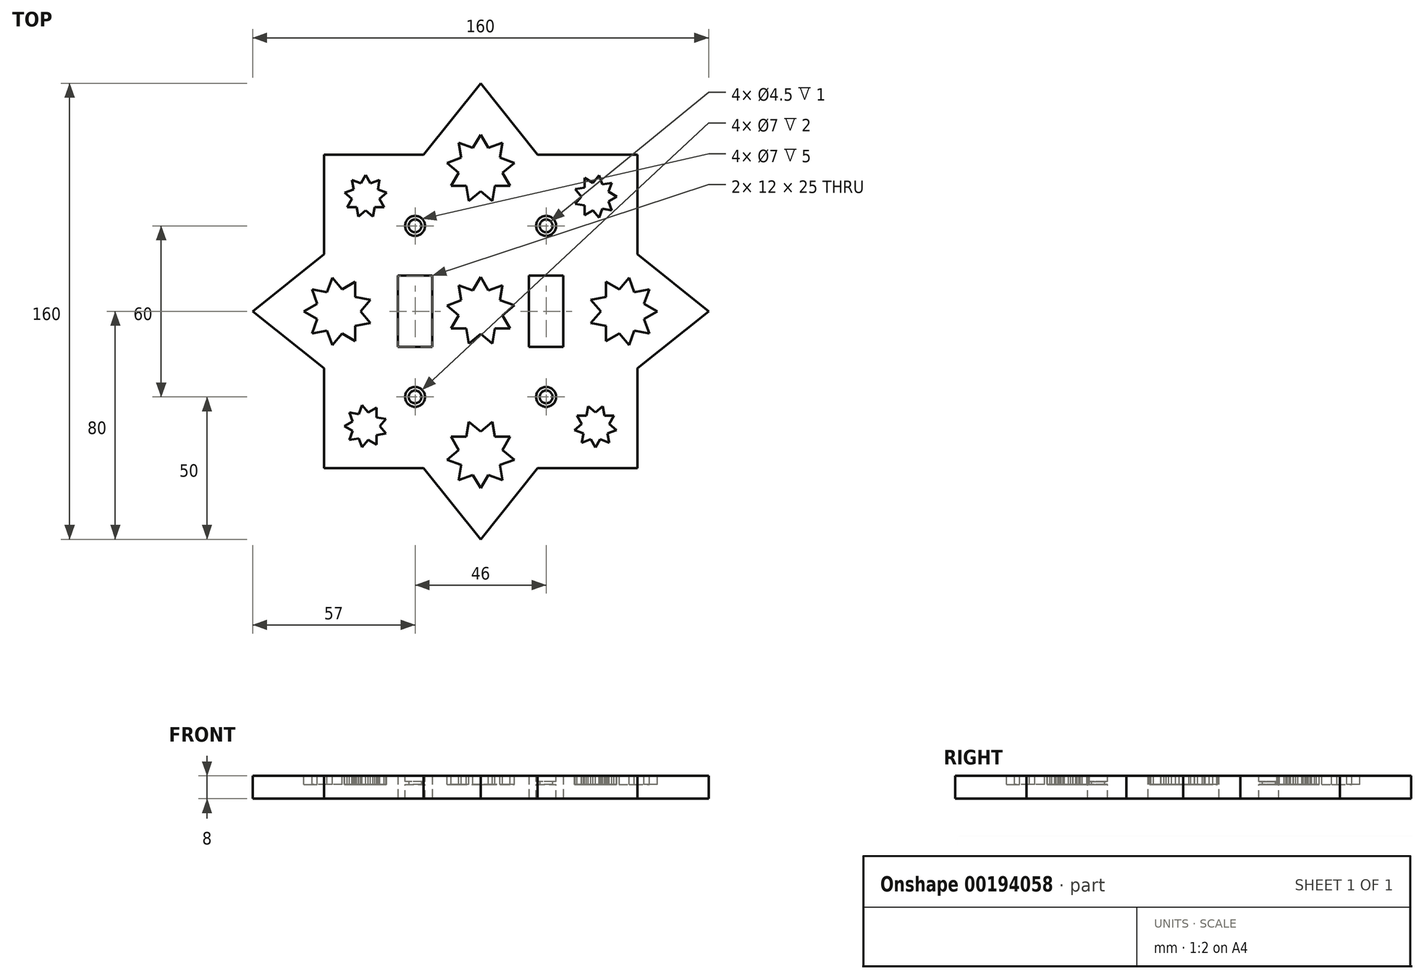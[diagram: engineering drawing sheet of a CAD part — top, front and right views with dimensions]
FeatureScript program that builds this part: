
annotation { "Feature Type Name" : "Feature", "Feature Type Description" : "" }
export const myFeature = defineFeature(function(context is Context, id is Id, definition is map)
    precondition{}
    {
        {
            var Q0;
            Q0=qCreatedBy(makeId("Top.planeOp"),FACE);
            var sketch = newSketch(context, id + "F0", { "sketchPlane" : qUnion([Q0])});
            skLineSegment(sketch, "E0.bottom", {"start": v(55, 55) * mm, "end": v(20, 55) * mm});
            skLineSegment(sketch, "E0.top", {"start": v(55, -55) * mm, "end": v(20, -55) * mm});
            skLineSegment(sketch, "E0.left", {"start": v(55, 55) * mm, "end": v(55, 20) * mm});
            skLineSegment(sketch, "E0.right", {"start": v(-55, 55) * mm, "end": v(-55, 20) * mm});
            skPoint(sketch, "E0.middle", {"position": v(0, 0) * mm});
            skCircle(sketch, "E1", {"center": v(-23, -30) * mm, "radius": 2.25 * mm});
            skCircle(sketch, "E2", {"center": v(-23, 30) * mm, "radius": 2.25 * mm});
            skLineSegment(sketch, "E3.bottom", {"start": v(-29, 12.5) * mm, "end": v(-17, 12.5) * mm});
            skLineSegment(sketch, "E3.top", {"start": v(-29, -12.5) * mm, "end": v(-17, -12.5) * mm});
            skLineSegment(sketch, "E3.left", {"start": v(-29, 12.5) * mm, "end": v(-29, -12.5) * mm});
            skLineSegment(sketch, "E3.right", {"start": v(-17, 12.5) * mm, "end": v(-17, -12.5) * mm});
            skLineSegment(sketch, "E4", {"start": v(-23, 30) * mm, "end": v(-23, -30) * mm, "construction": true});
            skLineSegment(sketch, "E5.MirrorCS", {"start": v(-17, -12.5) * mm, "end": v(-29, -12.5) * mm});
            skLineSegment(sketch, "E6.MirrorCS", {"start": v(-17, 12.5) * mm, "end": v(-29, 12.5) * mm});
            skCircle(sketch, "E7.MirrorC", {"center": v(23, 30) * mm, "radius": 2.25 * mm});
            skLineSegment(sketch, "E8.MirrorCS", {"start": v(29, 12.5) * mm, "end": v(29, -12.5) * mm});
            skLineSegment(sketch, "E9.MirrorCS", {"start": v(17, -12.5) * mm, "end": v(29, -12.5) * mm});
            skCircle(sketch, "E10.MirrorC", {"center": v(23, -30) * mm, "radius": 2.25 * mm});
            skLineSegment(sketch, "E11.MirrorCS", {"start": v(17, 12.5) * mm, "end": v(29, 12.5) * mm});
            skLineSegment(sketch, "E12.MirrorCS", {"start": v(17, 12.5) * mm, "end": v(17, -12.5) * mm});
            skLineSegment(sketch, "E13.MirrorCS", {"start": v(29, -12.5) * mm, "end": v(17, -12.5) * mm});
            skLineSegment(sketch, "E14.MirrorCS", {"start": v(29, 12.5) * mm, "end": v(17, 12.5) * mm});
            skLineSegment(sketch, "E15.MirrorCS", {"start": v(23, 30) * mm, "end": v(23, -30) * mm, "construction": true});
            skLineSegment(sketch, "E16", {"start": v(55, 20) * mm, "end": v(80, 0) * mm});
            skLineSegment(sketch, "E17", {"start": v(-20, 55) * mm, "end": v(0, 80) * mm});
            skLineSegment(sketch, "E18", {"start": v(0, 80) * mm, "end": v(20, 55) * mm});
            skLineSegment(sketch, "E19.MirrorCS", {"start": v(-20, -55) * mm, "end": v(0, -80) * mm});
            skLineSegment(sketch, "E20.MirrorCS", {"start": v(0, -80) * mm, "end": v(20, -55) * mm});
            skLineSegment(sketch, "E21.MirrorCS", {"start": v(55, -20) * mm, "end": v(80, 0) * mm});
            skLineSegment(sketch, "E22.MirrorCS", {"start": v(-55, 20) * mm, "end": v(-80, 0) * mm});
            skLineSegment(sketch, "E23.MirrorCS", {"start": v(-55, -20) * mm, "end": v(-80, 0) * mm});
            skLineSegment(sketch, "E24.trimOffspring", {"start": v(-55, -20) * mm, "end": v(-55, -55) * mm});
            skLineSegment(sketch, "E25.trimOffspring", {"start": v(55, -20) * mm, "end": v(55, -55) * mm});
            skLineSegment(sketch, "E26.trimOffspring", {"start": v(-20, -55) * mm, "end": v(-55, -55) * mm});
            skLineSegment(sketch, "E27.trimOffspring", {"start": v(-20, 55) * mm, "end": v(-55, 55) * mm});
            skPoint(sketch, "E28.MirrorCS.end.orphan", {"position": v(55, 34.57) * mm});
            skPoint(sketch, "E28.MirrorCS.start.orphan", {"position": v(80, 0) * mm});
            skPoint(sketch, "E29.orphan", {"position": v(55, -34.57) * mm});
            skSolve(sketch);
        }
        {
            var Q0;
            Q0 = qSketchRegion(id + "F0", true);
            extrude(context, id + "F1", {"entities" : qUnion([Q0]), "depth" : 3 * mm});
        }
        {
            var Q0;
            Q0=makeQuery(id+"F1.opExtrude","CAP_FACE",FACE,{"disambiguationData":[OSD([sQuery(id+"F0.wireOp",EDGE,"E0.bottom"),sQuery(id+"F0.wireOp",EDGE,"E0.top"),sQuery(id+"F0.wireOp",EDGE,"E0.left"),sQuery(id+"F0.wireOp",EDGE,"E0.right"),sQuery(id+"F0.wireOp",EDGE,"E1"),sQuery(id+"F0.wireOp",EDGE,"E2"),sQuery(id+"F0.wireOp",EDGE,"E3.right"),sQuery(id+"F0.wireOp",EDGE,"E5.MirrorCS"),sQuery(id+"F0.wireOp",EDGE,"E3.left"),sQuery(id+"F0.wireOp",EDGE,"E6.MirrorCS"),sQuery(id+"F0.wireOp",EDGE,"E10.MirrorC"),sQuery(id+"F0.wireOp",EDGE,"E14.MirrorCS"),sQuery(id+"F0.wireOp",EDGE,"E7.MirrorC"),sQuery(id+"F0.wireOp",EDGE,"E8.MirrorCS"),sQuery(id+"F0.wireOp",EDGE,"E9.MirrorCS"),sQuery(id+"F0.wireOp",EDGE,"E12.MirrorCS"),sQuery(id+"F0.wireOp",EDGE,"E16"),sQuery(id+"F0.wireOp",EDGE,"E17"),sQuery(id+"F0.wireOp",EDGE,"E18"),sQuery(id+"F0.wireOp",EDGE,"E19.MirrorCS"),sQuery(id+"F0.wireOp",EDGE,"E20.MirrorCS"),sQuery(id+"F0.wireOp",EDGE,"E21.MirrorCS"),sQuery(id+"F0.wireOp",EDGE,"E22.MirrorCS"),sQuery(id+"F0.wireOp",EDGE,"E23.MirrorCS"),sQuery(id+"F0.wireOp",EDGE,"E24.trimOffspring"),sQuery(id+"F0.wireOp",EDGE,"E25.trimOffspring"),sQuery(id+"F0.wireOp",EDGE,"E26.trimOffspring"),sQuery(id+"F0.wireOp",EDGE,"E27.trimOffspring")])],"isStart":false});
            var sketch = newSketch(context, id + "F2", { "sketchPlane" : qUnion([Q0])});
            skCircle(sketch, "E30.cCircle", {"center": v(0, 50) * mm, "radius": 6 * mm, "construction": true});
            skLineSegment(sketch, "E30.0", {"start": v(-10.4, 44) * mm, "end": v(-7.71, 48.64) * mm});
            skLineSegment(sketch, "E30.1", {"start": v(0, 62) * mm, "end": v(2.68, 57.36) * mm});
            skLineSegment(sketch, "E30.2", {"start": v(10.4, 44) * mm, "end": v(5.03, 44) * mm});
            skPoint(sketch, "E30.0.midPoint", {"position": v(-5.2, 53) * mm});
            skArc(sketch, "E31.cCircle", {"start": v(5.9, 48.96) * mm, "mid": v(-3.86, 54.6) * mm, "end": v(0, 44) * mm, "construction": true});
            skLineSegment(sketch, "E31.0", {"start": v(-11.82, 52.08) * mm, "end": v(-6.78, 53.92) * mm});
            skLineSegment(sketch, "E31.1", {"start": v(7.71, 59.2) * mm, "end": v(6.78, 53.92) * mm});
            skLineSegment(sketch, "E31.2", {"start": v(4.1, 38.72) * mm, "end": v(0, 42.17) * mm});
            skPoint(sketch, "E31.0.midPoint", {"position": v(-2.05, 55.64) * mm});
            skArc(sketch, "E32.cCircle", {"start": v(2.05, 55.64) * mm, "mid": v(0, 56) * mm, "end": v(-2.05, 55.64) * mm, "construction": true});
            skLineSegment(sketch, "E32.0", {"start": v(-7.71, 59.2) * mm, "end": v(-2.68, 57.36) * mm});
            skLineSegment(sketch, "E32.1", {"start": v(11.82, 52.08) * mm, "end": v(7.71, 48.64) * mm});
            skLineSegment(sketch, "E32.2", {"start": v(-4.1, 38.72) * mm, "end": v(-5.03, 44) * mm});
            skPoint(sketch, "E32.0.midPoint", {"position": v(2.05, 55.64) * mm});
            skLineSegment(sketch, "E33", {"start": v(0, 50) * mm, "end": v(0, 121.63) * mm, "construction": true});
            skLineSegment(sketch, "E34.trimOffspring", {"start": v(7.71, 48.64) * mm, "end": v(10.4, 44) * mm});
            skLineSegment(sketch, "E35.trimOffspring", {"start": v(6.78, 53.92) * mm, "end": v(11.82, 52.08) * mm});
            skLineSegment(sketch, "E36.trimOffspring", {"start": v(2.68, 57.36) * mm, "end": v(7.71, 59.2) * mm});
            skLineSegment(sketch, "E37.trimOffspring", {"start": v(-2.68, 57.36) * mm, "end": v(0, 62) * mm});
            skArc(sketch, "E38.trimOffspring", {"start": v(-5.2, 53) * mm, "mid": v(0, 44) * mm, "end": v(5.2, 53) * mm, "construction": true});
            skLineSegment(sketch, "E39.trimOffspring", {"start": v(-6.78, 53.92) * mm, "end": v(-7.71, 59.2) * mm});
            skLineSegment(sketch, "E40.trimOffspring", {"start": v(-7.71, 48.64) * mm, "end": v(-11.82, 52.08) * mm});
            skLineSegment(sketch, "E41.trimOffspring", {"start": v(-5.03, 44) * mm, "end": v(-10.4, 44) * mm});
            skLineSegment(sketch, "E42.trimOffspring", {"start": v(0, 42.17) * mm, "end": v(-4.1, 38.72) * mm});
            skLineSegment(sketch, "E43.trimOffspring", {"start": v(5.03, 44) * mm, "end": v(4.1, 38.72) * mm});
            skLineSegment(sketch, "E44.1.0", {"start": v(-59.2, -7.71) * mm, "end": v(-57.36, -2.68) * mm});
            skLineSegment(sketch, "E44.1.1", {"start": v(-59.2, 7.71) * mm, "end": v(-53.92, 6.78) * mm});
            skLineSegment(sketch, "E44.1.2", {"start": v(-48.64, 7.71) * mm, "end": v(-44, 10.4) * mm});
            skPoint(sketch, "E44.1.3", {"position": v(-55.64, -2.05) * mm});
            skLineSegment(sketch, "E44.1.4", {"start": v(-52.08, -11.82) * mm, "end": v(-53.92, -6.78) * mm});
            skLineSegment(sketch, "E44.1.5", {"start": v(-44, -5.03) * mm, "end": v(-44, -10.4) * mm});
            skArc(sketch, "E44.1.6", {"start": v(-48.96, 5.9) * mm, "mid": v(-54.6, -3.86) * mm, "end": v(-44, 0) * mm, "construction": true});
            skLineSegment(sketch, "E44.1.7", {"start": v(-53.92, 6.78) * mm, "end": v(-52.08, 11.82) * mm});
            skPoint(sketch, "E44.1.8", {"position": v(-53, -5.2) * mm});
            skLineSegment(sketch, "E44.1.9", {"start": v(-44, 10.4) * mm, "end": v(-44, 5.03) * mm});
            skLineSegment(sketch, "E44.1.10", {"start": v(-48.64, -7.71) * mm, "end": v(-52.08, -11.82) * mm});
            skLineSegment(sketch, "E44.1.11", {"start": v(-44, -10.4) * mm, "end": v(-48.64, -7.71) * mm});
            skCircle(sketch, "E44.1.12", {"center": v(-50, 0) * mm, "radius": 6 * mm, "construction": true});
            skLineSegment(sketch, "E44.1.13", {"start": v(-38.72, -4.1) * mm, "end": v(-44, -5.03) * mm});
            skLineSegment(sketch, "E44.1.14", {"start": v(-44, 5.03) * mm, "end": v(-38.72, 4.1) * mm});
            skLineSegment(sketch, "E44.1.15", {"start": v(-57.36, 2.68) * mm, "end": v(-59.2, 7.71) * mm});
            skLineSegment(sketch, "E44.1.16", {"start": v(-42.17, 0) * mm, "end": v(-38.72, -4.1) * mm});
            skLineSegment(sketch, "E44.1.17", {"start": v(-52.08, 11.82) * mm, "end": v(-48.64, 7.71) * mm});
            skPoint(sketch, "E44.1.18", {"position": v(-55.64, 2.05) * mm});
            skArc(sketch, "E44.1.19", {"start": v(-55.64, 2.05) * mm, "mid": v(-56, 0) * mm, "end": v(-55.64, -2.05) * mm, "construction": true});
            skArc(sketch, "E44.1.20", {"start": v(-53, -5.2) * mm, "mid": v(-44, 0) * mm, "end": v(-53, 5.2) * mm, "construction": true});
            skLineSegment(sketch, "E44.1.21", {"start": v(-62, 0) * mm, "end": v(-57.36, 2.68) * mm});
            skLineSegment(sketch, "E44.1.22", {"start": v(-53.92, -6.78) * mm, "end": v(-59.2, -7.71) * mm});
            skLineSegment(sketch, "E44.1.23", {"start": v(-57.36, -2.68) * mm, "end": v(-62, 0) * mm});
            skLineSegment(sketch, "E44.1.24", {"start": v(-38.72, 4.1) * mm, "end": v(-42.17, 0) * mm});
            skLineSegment(sketch, "E44.2.0", {"start": v(7.71, -59.2) * mm, "end": v(2.68, -57.36) * mm});
            skLineSegment(sketch, "E44.2.1", {"start": v(-7.71, -59.2) * mm, "end": v(-6.78, -53.92) * mm});
            skLineSegment(sketch, "E44.2.2", {"start": v(-7.71, -48.64) * mm, "end": v(-10.4, -44) * mm});
            skPoint(sketch, "E44.2.3", {"position": v(2.05, -55.64) * mm});
            skLineSegment(sketch, "E44.2.4", {"start": v(11.82, -52.08) * mm, "end": v(6.78, -53.92) * mm});
            skLineSegment(sketch, "E44.2.5", {"start": v(5.03, -44) * mm, "end": v(10.4, -44) * mm});
            skArc(sketch, "E44.2.6", {"start": v(-5.9, -48.96) * mm, "mid": v(3.86, -54.6) * mm, "end": v(0, -44) * mm, "construction": true});
            skLineSegment(sketch, "E44.2.7", {"start": v(-6.78, -53.92) * mm, "end": v(-11.82, -52.08) * mm});
            skPoint(sketch, "E44.2.8", {"position": v(5.2, -53) * mm});
            skLineSegment(sketch, "E44.2.9", {"start": v(-10.4, -44) * mm, "end": v(-5.03, -44) * mm});
            skLineSegment(sketch, "E44.2.10", {"start": v(7.71, -48.64) * mm, "end": v(11.82, -52.08) * mm});
            skLineSegment(sketch, "E44.2.11", {"start": v(10.4, -44) * mm, "end": v(7.71, -48.64) * mm});
            skCircle(sketch, "E44.2.12", {"center": v(0, -50) * mm, "radius": 6 * mm, "construction": true});
            skLineSegment(sketch, "E44.2.13", {"start": v(4.1, -38.72) * mm, "end": v(5.03, -44) * mm});
            skLineSegment(sketch, "E44.2.14", {"start": v(-5.03, -44) * mm, "end": v(-4.1, -38.72) * mm});
            skLineSegment(sketch, "E44.2.15", {"start": v(-2.68, -57.36) * mm, "end": v(-7.71, -59.2) * mm});
            skLineSegment(sketch, "E44.2.16", {"start": v(0, -42.17) * mm, "end": v(4.1, -38.72) * mm});
            skLineSegment(sketch, "E44.2.17", {"start": v(-11.82, -52.08) * mm, "end": v(-7.71, -48.64) * mm});
            skPoint(sketch, "E44.2.18", {"position": v(-2.05, -55.64) * mm});
            skArc(sketch, "E44.2.19", {"start": v(-2.05, -55.64) * mm, "mid": v(0, -56) * mm, "end": v(2.05, -55.64) * mm, "construction": true});
            skArc(sketch, "E44.2.20", {"start": v(5.2, -53) * mm, "mid": v(0, -44) * mm, "end": v(-5.2, -53) * mm, "construction": true});
            skLineSegment(sketch, "E44.2.21", {"start": v(0, -62) * mm, "end": v(-2.68, -57.36) * mm});
            skLineSegment(sketch, "E44.2.22", {"start": v(6.78, -53.92) * mm, "end": v(7.71, -59.2) * mm});
            skLineSegment(sketch, "E44.2.23", {"start": v(2.68, -57.36) * mm, "end": v(0, -62) * mm});
            skLineSegment(sketch, "E44.2.24", {"start": v(-4.1, -38.72) * mm, "end": v(0, -42.17) * mm});
            skLineSegment(sketch, "E44.3.0", {"start": v(59.2, 7.71) * mm, "end": v(57.36, 2.68) * mm});
            skLineSegment(sketch, "E44.3.1", {"start": v(59.2, -7.71) * mm, "end": v(53.92, -6.78) * mm});
            skLineSegment(sketch, "E44.3.2", {"start": v(48.64, -7.71) * mm, "end": v(44, -10.4) * mm});
            skPoint(sketch, "E44.3.3", {"position": v(55.64, 2.05) * mm});
            skLineSegment(sketch, "E44.3.4", {"start": v(52.08, 11.82) * mm, "end": v(53.92, 6.78) * mm});
            skLineSegment(sketch, "E44.3.5", {"start": v(44, 5.03) * mm, "end": v(44, 10.4) * mm});
            skArc(sketch, "E44.3.6", {"start": v(48.96, -5.9) * mm, "mid": v(54.6, 3.86) * mm, "end": v(44, 0) * mm, "construction": true});
            skLineSegment(sketch, "E44.3.7", {"start": v(53.92, -6.78) * mm, "end": v(52.08, -11.82) * mm});
            skPoint(sketch, "E44.3.8", {"position": v(53, 5.2) * mm});
            skLineSegment(sketch, "E44.3.9", {"start": v(44, -10.4) * mm, "end": v(44, -5.03) * mm});
            skLineSegment(sketch, "E44.3.10", {"start": v(48.64, 7.71) * mm, "end": v(52.08, 11.82) * mm});
            skLineSegment(sketch, "E44.3.11", {"start": v(44, 10.4) * mm, "end": v(48.64, 7.71) * mm});
            skCircle(sketch, "E44.3.12", {"center": v(50, 0) * mm, "radius": 6 * mm, "construction": true});
            skLineSegment(sketch, "E44.3.13", {"start": v(38.72, 4.1) * mm, "end": v(44, 5.03) * mm});
            skLineSegment(sketch, "E44.3.14", {"start": v(44, -5.03) * mm, "end": v(38.72, -4.1) * mm});
            skLineSegment(sketch, "E44.3.15", {"start": v(57.36, -2.68) * mm, "end": v(59.2, -7.71) * mm});
            skLineSegment(sketch, "E44.3.16", {"start": v(42.17, 0) * mm, "end": v(38.72, 4.1) * mm});
            skLineSegment(sketch, "E44.3.17", {"start": v(52.08, -11.82) * mm, "end": v(48.64, -7.71) * mm});
            skPoint(sketch, "E44.3.18", {"position": v(55.64, -2.05) * mm});
            skArc(sketch, "E44.3.19", {"start": v(55.64, -2.05) * mm, "mid": v(56, 0) * mm, "end": v(55.64, 2.05) * mm, "construction": true});
            skArc(sketch, "E44.3.20", {"start": v(53, 5.2) * mm, "mid": v(44, 0) * mm, "end": v(53, -5.2) * mm, "construction": true});
            skLineSegment(sketch, "E44.3.21", {"start": v(62, 0) * mm, "end": v(57.36, -2.68) * mm});
            skLineSegment(sketch, "E44.3.22", {"start": v(53.92, 6.78) * mm, "end": v(59.2, 7.71) * mm});
            skLineSegment(sketch, "E44.3.23", {"start": v(57.36, 2.68) * mm, "end": v(62, 0) * mm});
            skLineSegment(sketch, "E44.3.24", {"start": v(38.72, -4.1) * mm, "end": v(42.17, 0) * mm});
            skPoint(sketch, "E44.center", {"position": v(0, 0) * mm});
            skCircle(sketch, "E45.cCircle", {"center": v(-40.3, 40.3) * mm, "radius": 3.75 * mm, "construction": true});
            skLineSegment(sketch, "E45.0", {"start": v(-46.8, 36.56) * mm, "end": v(-45.13, 39.46) * mm});
            skLineSegment(sketch, "E45.1", {"start": v(-40.3, 47.8) * mm, "end": v(-38.63, 44.9) * mm});
            skLineSegment(sketch, "E45.2", {"start": v(-33.8, 36.56) * mm, "end": v(-37.16, 36.56) * mm});
            skPoint(sketch, "E45.0.midPoint", {"position": v(-43.55, 42.18) * mm});
            skArc(sketch, "E46.cCircle", {"start": v(-36.61, 39.65) * mm, "mid": v(-43.7, 41.9) * mm, "end": v(-37.43, 37.9) * mm, "construction": true});
            skLineSegment(sketch, "E46.0", {"start": v(-47.7, 41.6) * mm, "end": v(-44.54, 42.75) * mm});
            skLineSegment(sketch, "E46.1", {"start": v(-35.48, 46.05) * mm, "end": v(-36.07, 42.75) * mm});
            skLineSegment(sketch, "E46.2", {"start": v(-37.74, 33.26) * mm, "end": v(-40.3, 35.4) * mm});
            skPoint(sketch, "E46.0.midPoint", {"position": v(-41.59, 43.83) * mm});
            skArc(sketch, "E47.cCircle", {"start": v(-39.02, 43.83) * mm, "mid": v(-40.3, 44.06) * mm, "end": v(-41.59, 43.83) * mm, "construction": true});
            skLineSegment(sketch, "E47.0", {"start": v(-45.13, 46.05) * mm, "end": v(-41.98, 44.9) * mm});
            skLineSegment(sketch, "E47.1", {"start": v(-32.92, 41.6) * mm, "end": v(-35.48, 39.46) * mm});
            skLineSegment(sketch, "E47.2", {"start": v(-42.87, 33.26) * mm, "end": v(-43.45, 36.56) * mm});
            skPoint(sketch, "E47.0.midPoint", {"position": v(-39.02, 43.83) * mm});
            skLineSegment(sketch, "E48", {"start": v(-40.3, 40.3) * mm, "end": v(-40.3, 75.93) * mm, "construction": true});
            skLineSegment(sketch, "E49.trimOffspring", {"start": v(-35.48, 39.46) * mm, "end": v(-33.8, 36.56) * mm});
            skLineSegment(sketch, "E50.trimOffspring", {"start": v(-36.07, 42.75) * mm, "end": v(-32.92, 41.6) * mm});
            skLineSegment(sketch, "E51.trimOffspring", {"start": v(-38.63, 44.9) * mm, "end": v(-35.48, 46.05) * mm});
            skLineSegment(sketch, "E52.trimOffspring", {"start": v(-41.98, 44.9) * mm, "end": v(-40.3, 47.8) * mm});
            skArc(sketch, "E53.trimOffspring", {"start": v(-43.55, 42.18) * mm, "mid": v(-40.3, 36.56) * mm, "end": v(-37.06, 42.18) * mm, "construction": true});
            skLineSegment(sketch, "E54.trimOffspring", {"start": v(-44.54, 42.75) * mm, "end": v(-45.13, 46.05) * mm});
            skLineSegment(sketch, "E55.trimOffspring", {"start": v(-45.13, 39.46) * mm, "end": v(-47.7, 41.6) * mm});
            skLineSegment(sketch, "E56.trimOffspring", {"start": v(-43.45, 36.56) * mm, "end": v(-46.8, 36.56) * mm});
            skLineSegment(sketch, "E57.trimOffspring", {"start": v(-40.3, 35.4) * mm, "end": v(-42.87, 33.26) * mm});
            skLineSegment(sketch, "E58.trimOffspring", {"start": v(-37.16, 36.56) * mm, "end": v(-37.74, 33.26) * mm});
            skLineSegment(sketch, "E59", {"start": v(0, 0) * mm, "end": v(-55, 55) * mm, "construction": true});
            skLineSegment(sketch, "E60.1.0", {"start": v(-39.46, -45.13) * mm, "end": v(-41.6, -47.7) * mm});
            skLineSegment(sketch, "E60.1.1", {"start": v(-44.9, -38.63) * mm, "end": v(-46.05, -35.48) * mm});
            skPoint(sketch, "E60.1.2", {"position": v(-43.83, -39.02) * mm});
            skCircle(sketch, "E60.1.3", {"center": v(-40.3, -40.3) * mm, "radius": 3.75 * mm, "construction": true});
            skLineSegment(sketch, "E60.1.4", {"start": v(-41.6, -32.92) * mm, "end": v(-39.46, -35.48) * mm});
            skLineSegment(sketch, "E60.1.5", {"start": v(-46.05, -45.13) * mm, "end": v(-44.9, -41.98) * mm});
            skLineSegment(sketch, "E60.1.6", {"start": v(-44.9, -41.98) * mm, "end": v(-47.8, -40.3) * mm});
            skLineSegment(sketch, "E60.1.7", {"start": v(-36.56, -46.8) * mm, "end": v(-39.46, -45.13) * mm});
            skLineSegment(sketch, "E60.1.8", {"start": v(0, 0) * mm, "end": v(-55, -55) * mm, "construction": true});
            skLineSegment(sketch, "E60.1.9", {"start": v(-36.56, -33.8) * mm, "end": v(-36.56, -37.16) * mm});
            skLineSegment(sketch, "E60.1.10", {"start": v(-33.26, -37.74) * mm, "end": v(-35.4, -40.3) * mm});
            skLineSegment(sketch, "E60.1.11", {"start": v(-36.56, -37.16) * mm, "end": v(-33.26, -37.74) * mm});
            skLineSegment(sketch, "E60.1.12", {"start": v(-41.6, -47.7) * mm, "end": v(-42.75, -44.54) * mm});
            skLineSegment(sketch, "E60.1.13", {"start": v(-46.05, -35.48) * mm, "end": v(-42.75, -36.07) * mm});
            skLineSegment(sketch, "E60.1.14", {"start": v(-39.46, -35.48) * mm, "end": v(-36.56, -33.8) * mm});
            skLineSegment(sketch, "E60.1.15", {"start": v(-42.75, -36.07) * mm, "end": v(-41.6, -32.92) * mm});
            skPoint(sketch, "E60.1.16", {"position": v(-42.18, -43.55) * mm});
            skLineSegment(sketch, "E60.1.17", {"start": v(-40.3, -40.3) * mm, "end": v(-75.93, -40.3) * mm, "construction": true});
            skPoint(sketch, "E60.1.18", {"position": v(-43.83, -41.59) * mm});
            skLineSegment(sketch, "E60.1.19", {"start": v(-47.8, -40.3) * mm, "end": v(-44.9, -38.63) * mm});
            skLineSegment(sketch, "E60.1.20", {"start": v(-35.4, -40.3) * mm, "end": v(-33.26, -42.87) * mm});
            skLineSegment(sketch, "E60.1.21", {"start": v(-42.75, -44.54) * mm, "end": v(-46.05, -45.13) * mm});
            skLineSegment(sketch, "E60.1.22", {"start": v(-33.26, -42.87) * mm, "end": v(-36.56, -43.45) * mm});
            skLineSegment(sketch, "E60.1.23", {"start": v(-36.56, -43.45) * mm, "end": v(-36.56, -46.8) * mm});
            skArc(sketch, "E60.1.24", {"start": v(-42.18, -43.55) * mm, "mid": v(-36.56, -40.3) * mm, "end": v(-42.18, -37.06) * mm, "construction": true});
            skArc(sketch, "E60.1.25", {"start": v(-43.83, -39.02) * mm, "mid": v(-44.06, -40.3) * mm, "end": v(-43.83, -41.59) * mm, "construction": true});
            skArc(sketch, "E60.1.26", {"start": v(-39.65, -36.61) * mm, "mid": v(-41.9, -43.7) * mm, "end": v(-37.9, -37.43) * mm, "construction": true});
            skLineSegment(sketch, "E60.2.0", {"start": v(45.13, -39.46) * mm, "end": v(47.7, -41.6) * mm});
            skLineSegment(sketch, "E60.2.1", {"start": v(38.63, -44.9) * mm, "end": v(35.48, -46.05) * mm});
            skPoint(sketch, "E60.2.2", {"position": v(39.02, -43.83) * mm});
            skCircle(sketch, "E60.2.3", {"center": v(40.3, -40.3) * mm, "radius": 3.75 * mm, "construction": true});
            skLineSegment(sketch, "E60.2.4", {"start": v(32.92, -41.6) * mm, "end": v(35.48, -39.46) * mm});
            skLineSegment(sketch, "E60.2.5", {"start": v(45.13, -46.05) * mm, "end": v(41.98, -44.9) * mm});
            skLineSegment(sketch, "E60.2.6", {"start": v(41.98, -44.9) * mm, "end": v(40.3, -47.8) * mm});
            skLineSegment(sketch, "E60.2.7", {"start": v(46.8, -36.56) * mm, "end": v(45.13, -39.46) * mm});
            skLineSegment(sketch, "E60.2.8", {"start": v(0, 0) * mm, "end": v(55, -55) * mm, "construction": true});
            skLineSegment(sketch, "E60.2.9", {"start": v(33.8, -36.56) * mm, "end": v(37.16, -36.56) * mm});
            skLineSegment(sketch, "E60.2.10", {"start": v(37.74, -33.26) * mm, "end": v(40.3, -35.4) * mm});
            skLineSegment(sketch, "E60.2.11", {"start": v(37.16, -36.56) * mm, "end": v(37.74, -33.26) * mm});
            skLineSegment(sketch, "E60.2.12", {"start": v(47.7, -41.6) * mm, "end": v(44.54, -42.75) * mm});
            skLineSegment(sketch, "E60.2.13", {"start": v(35.48, -46.05) * mm, "end": v(36.07, -42.75) * mm});
            skLineSegment(sketch, "E60.2.14", {"start": v(35.48, -39.46) * mm, "end": v(33.8, -36.56) * mm});
            skLineSegment(sketch, "E60.2.15", {"start": v(36.07, -42.75) * mm, "end": v(32.92, -41.6) * mm});
            skPoint(sketch, "E60.2.16", {"position": v(43.55, -42.18) * mm});
            skLineSegment(sketch, "E60.2.17", {"start": v(40.3, -40.3) * mm, "end": v(40.3, -75.93) * mm, "construction": true});
            skPoint(sketch, "E60.2.18", {"position": v(41.59, -43.83) * mm});
            skLineSegment(sketch, "E60.2.19", {"start": v(40.3, -47.8) * mm, "end": v(38.63, -44.9) * mm});
            skLineSegment(sketch, "E60.2.20", {"start": v(40.3, -35.4) * mm, "end": v(42.87, -33.26) * mm});
            skLineSegment(sketch, "E60.2.21", {"start": v(44.54, -42.75) * mm, "end": v(45.13, -46.05) * mm});
            skLineSegment(sketch, "E60.2.22", {"start": v(42.87, -33.26) * mm, "end": v(43.45, -36.56) * mm});
            skLineSegment(sketch, "E60.2.23", {"start": v(43.45, -36.56) * mm, "end": v(46.8, -36.56) * mm});
            skArc(sketch, "E60.2.24", {"start": v(43.55, -42.18) * mm, "mid": v(40.3, -36.56) * mm, "end": v(37.06, -42.18) * mm, "construction": true});
            skArc(sketch, "E60.2.25", {"start": v(39.02, -43.83) * mm, "mid": v(40.3, -44.06) * mm, "end": v(41.59, -43.83) * mm, "construction": true});
            skArc(sketch, "E60.2.26", {"start": v(36.61, -39.65) * mm, "mid": v(43.7, -41.9) * mm, "end": v(37.43, -37.9) * mm, "construction": true});
            skLineSegment(sketch, "E60.3.0", {"start": v(39.46, 45.13) * mm, "end": v(41.6, 47.7) * mm});
            skLineSegment(sketch, "E60.3.1", {"start": v(44.9, 38.63) * mm, "end": v(46.05, 35.48) * mm});
            skPoint(sketch, "E60.3.2", {"position": v(43.83, 39.02) * mm});
            skCircle(sketch, "E60.3.3", {"center": v(40.3, 40.3) * mm, "radius": 3.75 * mm, "construction": true});
            skLineSegment(sketch, "E60.3.4", {"start": v(41.6, 32.92) * mm, "end": v(39.46, 35.48) * mm});
            skLineSegment(sketch, "E60.3.5", {"start": v(46.05, 45.13) * mm, "end": v(44.9, 41.98) * mm});
            skLineSegment(sketch, "E60.3.6", {"start": v(44.9, 41.98) * mm, "end": v(47.8, 40.3) * mm});
            skLineSegment(sketch, "E60.3.7", {"start": v(36.56, 46.8) * mm, "end": v(39.46, 45.13) * mm});
            skLineSegment(sketch, "E60.3.8", {"start": v(0, 0) * mm, "end": v(55, 55) * mm, "construction": true});
            skLineSegment(sketch, "E60.3.9", {"start": v(36.56, 33.8) * mm, "end": v(36.56, 37.16) * mm});
            skLineSegment(sketch, "E60.3.10", {"start": v(33.26, 37.74) * mm, "end": v(35.4, 40.3) * mm});
            skLineSegment(sketch, "E60.3.11", {"start": v(36.56, 37.16) * mm, "end": v(33.26, 37.74) * mm});
            skLineSegment(sketch, "E60.3.12", {"start": v(41.6, 47.7) * mm, "end": v(42.75, 44.54) * mm});
            skLineSegment(sketch, "E60.3.13", {"start": v(46.05, 35.48) * mm, "end": v(42.75, 36.07) * mm});
            skLineSegment(sketch, "E60.3.14", {"start": v(39.46, 35.48) * mm, "end": v(36.56, 33.8) * mm});
            skLineSegment(sketch, "E60.3.15", {"start": v(42.75, 36.07) * mm, "end": v(41.6, 32.92) * mm});
            skPoint(sketch, "E60.3.16", {"position": v(42.18, 43.55) * mm});
            skLineSegment(sketch, "E60.3.17", {"start": v(40.3, 40.3) * mm, "end": v(75.93, 40.3) * mm, "construction": true});
            skPoint(sketch, "E60.3.18", {"position": v(43.83, 41.59) * mm});
            skLineSegment(sketch, "E60.3.19", {"start": v(47.8, 40.3) * mm, "end": v(44.9, 38.63) * mm});
            skLineSegment(sketch, "E60.3.20", {"start": v(35.4, 40.3) * mm, "end": v(33.26, 42.87) * mm});
            skLineSegment(sketch, "E60.3.21", {"start": v(42.75, 44.54) * mm, "end": v(46.05, 45.13) * mm});
            skLineSegment(sketch, "E60.3.22", {"start": v(33.26, 42.87) * mm, "end": v(36.56, 43.45) * mm});
            skLineSegment(sketch, "E60.3.23", {"start": v(36.56, 43.45) * mm, "end": v(36.56, 46.8) * mm});
            skArc(sketch, "E60.3.24", {"start": v(42.18, 43.55) * mm, "mid": v(36.56, 40.3) * mm, "end": v(42.18, 37.06) * mm, "construction": true});
            skArc(sketch, "E60.3.25", {"start": v(43.83, 39.02) * mm, "mid": v(44.06, 40.3) * mm, "end": v(43.83, 41.59) * mm, "construction": true});
            skArc(sketch, "E60.3.26", {"start": v(39.65, 36.61) * mm, "mid": v(41.9, 43.7) * mm, "end": v(37.9, 37.43) * mm, "construction": true});
            skCircle(sketch, "E61.cCircle", {"center": v(0, 0) * mm, "radius": 6 * mm, "construction": true});
            skLineSegment(sketch, "E61.0", {"start": v(-10.4, -6) * mm, "end": v(-7.71, -1.36) * mm});
            skLineSegment(sketch, "E61.1", {"start": v(0, 12) * mm, "end": v(2.68, 7.36) * mm});
            skLineSegment(sketch, "E61.2", {"start": v(10.4, -6) * mm, "end": v(5.04, -6) * mm});
            skPoint(sketch, "E61.0.midPoint", {"position": v(-5.2, 3) * mm});
            skArc(sketch, "E62.cCircle", {"start": v(5.9, -1.04) * mm, "mid": v(5.65, 2) * mm, "end": v(3.93, 4.54) * mm, "construction": true});
            skLineSegment(sketch, "E62.0", {"start": v(-11.82, 2.08) * mm, "end": v(-6.78, 3.91) * mm});
            skLineSegment(sketch, "E62.1", {"start": v(7.71, 9.2) * mm, "end": v(6.78, 3.92) * mm});
            skLineSegment(sketch, "E62.2", {"start": v(4.1, -11.28) * mm, "end": v(0, -7.83) * mm});
            skPoint(sketch, "E62.0.midPoint", {"position": v(-2.05, 5.64) * mm});
            skArc(sketch, "E63.cCircle", {"start": v(2.05, 5.64) * mm, "mid": v(0, 6) * mm, "end": v(-2.05, 5.64) * mm, "construction": true});
            skLineSegment(sketch, "E63.0", {"start": v(-7.72, 9.2) * mm, "end": v(-2.68, 7.36) * mm});
            skLineSegment(sketch, "E63.1", {"start": v(11.82, 2.09) * mm, "end": v(7.71, -1.36) * mm});
            skLineSegment(sketch, "E63.2", {"start": v(-4.1, -11.28) * mm, "end": v(-5.03, -6) * mm});
            skPoint(sketch, "E63.0.midPoint", {"position": v(2.05, 5.64) * mm});
            skLineSegment(sketch, "E64.trimOffspring", {"start": v(7.71, -1.36) * mm, "end": v(10.4, -6) * mm});
            skLineSegment(sketch, "E65.trimOffspring", {"start": v(6.78, 3.92) * mm, "end": v(11.82, 2.09) * mm});
            skLineSegment(sketch, "E66.trimOffspring", {"start": v(2.68, 7.36) * mm, "end": v(7.71, 9.2) * mm});
            skLineSegment(sketch, "E67.trimOffspring", {"start": v(-2.68, 7.36) * mm, "end": v(0, 12) * mm});
            skArc(sketch, "E68.trimOffspring", {"start": v(-5.2, 3) * mm, "mid": v(0, -6) * mm, "end": v(5.2, 3) * mm, "construction": true});
            skLineSegment(sketch, "E69.trimOffspring", {"start": v(-6.78, 3.91) * mm, "end": v(-7.72, 9.2) * mm});
            skLineSegment(sketch, "E70.trimOffspring", {"start": v(-7.71, -1.36) * mm, "end": v(-11.82, 2.08) * mm});
            skLineSegment(sketch, "E71.trimOffspring", {"start": v(-5.03, -6) * mm, "end": v(-10.4, -6) * mm});
            skLineSegment(sketch, "E72.trimOffspring", {"start": v(0, -7.83) * mm, "end": v(-4.1, -11.28) * mm});
            skLineSegment(sketch, "E73.trimOffspring", {"start": v(5.04, -6) * mm, "end": v(4.1, -11.28) * mm});
            skSolve(sketch);
        }
        {
            var Q0;
            Q0 = qSketchRegion(id + "F2", true);
            extrude(context, id + "F3", {"entities" : qUnion([Q0]), "operationType" : NewBodyOperationType.REMOVE, "oppositeDirection" : true, "depth" : 25 * mm});
        }
        {
            var Q0;
            Q0=makeQuery(id+"F1.opExtrude","CAP_FACE",FACE,{"disambiguationData":[OSD([sQuery(id+"F0.wireOp",EDGE,"E0.bottom"),sQuery(id+"F0.wireOp",EDGE,"E0.top"),sQuery(id+"F0.wireOp",EDGE,"E0.left"),sQuery(id+"F0.wireOp",EDGE,"E0.right"),sQuery(id+"F0.wireOp",EDGE,"E1"),sQuery(id+"F0.wireOp",EDGE,"E2"),sQuery(id+"F0.wireOp",EDGE,"E3.right"),sQuery(id+"F0.wireOp",EDGE,"E5.MirrorCS"),sQuery(id+"F0.wireOp",EDGE,"E3.left"),sQuery(id+"F0.wireOp",EDGE,"E6.MirrorCS"),sQuery(id+"F0.wireOp",EDGE,"E10.MirrorC"),sQuery(id+"F0.wireOp",EDGE,"E14.MirrorCS"),sQuery(id+"F0.wireOp",EDGE,"E7.MirrorC"),sQuery(id+"F0.wireOp",EDGE,"E8.MirrorCS"),sQuery(id+"F0.wireOp",EDGE,"E9.MirrorCS"),sQuery(id+"F0.wireOp",EDGE,"E12.MirrorCS"),sQuery(id+"F0.wireOp",EDGE,"E16"),sQuery(id+"F0.wireOp",EDGE,"E17"),sQuery(id+"F0.wireOp",EDGE,"E18"),sQuery(id+"F0.wireOp",EDGE,"E19.MirrorCS"),sQuery(id+"F0.wireOp",EDGE,"E20.MirrorCS"),sQuery(id+"F0.wireOp",EDGE,"E21.MirrorCS"),sQuery(id+"F0.wireOp",EDGE,"E22.MirrorCS"),sQuery(id+"F0.wireOp",EDGE,"E23.MirrorCS"),sQuery(id+"F0.wireOp",EDGE,"E24.trimOffspring"),sQuery(id+"F0.wireOp",EDGE,"E25.trimOffspring"),sQuery(id+"F0.wireOp",EDGE,"E26.trimOffspring"),sQuery(id+"F0.wireOp",EDGE,"E27.trimOffspring")])],"isStart":false});
            var sketch = newSketch(context, id + "F4", { "sketchPlane" : qUnion([Q0])});
            skCircle(sketch, "E74", {"center": v(-23, 30) * mm, "radius": 3.5 * mm});
            skCircle(sketch, "E75", {"center": v(23, 30) * mm, "radius": 3.5 * mm});
            skCircle(sketch, "E76", {"center": v(23, -30) * mm, "radius": 3.5 * mm});
            skCircle(sketch, "E77", {"center": v(-23, -30) * mm, "radius": 3.5 * mm});
            skSolve(sketch);
        }
        {
            var Q0;
            Q0 = qSketchRegion(id + "F4", true);
            extrude(context, id + "F5", {"entities" : qUnion([Q0]), "operationType" : NewBodyOperationType.REMOVE, "oppositeDirection" : true, "depth" : 2 * mm});
        }
        {
            var Q0;
            Q0=makeQuery(id+"F1.opExtrude","CAP_FACE",FACE,{"disambiguationData":[OSD([sQuery(id+"F0.wireOp",EDGE,"E0.bottom"),sQuery(id+"F0.wireOp",EDGE,"E0.top"),sQuery(id+"F0.wireOp",EDGE,"E0.left"),sQuery(id+"F0.wireOp",EDGE,"E0.right"),sQuery(id+"F0.wireOp",EDGE,"E1"),sQuery(id+"F0.wireOp",EDGE,"E2"),sQuery(id+"F0.wireOp",EDGE,"E3.right"),sQuery(id+"F0.wireOp",EDGE,"E5.MirrorCS"),sQuery(id+"F0.wireOp",EDGE,"E3.left"),sQuery(id+"F0.wireOp",EDGE,"E6.MirrorCS"),sQuery(id+"F0.wireOp",EDGE,"E10.MirrorC"),sQuery(id+"F0.wireOp",EDGE,"E14.MirrorCS"),sQuery(id+"F0.wireOp",EDGE,"E7.MirrorC"),sQuery(id+"F0.wireOp",EDGE,"E8.MirrorCS"),sQuery(id+"F0.wireOp",EDGE,"E9.MirrorCS"),sQuery(id+"F0.wireOp",EDGE,"E12.MirrorCS"),sQuery(id+"F0.wireOp",EDGE,"E16"),sQuery(id+"F0.wireOp",EDGE,"E17"),sQuery(id+"F0.wireOp",EDGE,"E18"),sQuery(id+"F0.wireOp",EDGE,"E19.MirrorCS"),sQuery(id+"F0.wireOp",EDGE,"E20.MirrorCS"),sQuery(id+"F0.wireOp",EDGE,"E21.MirrorCS"),sQuery(id+"F0.wireOp",EDGE,"E22.MirrorCS"),sQuery(id+"F0.wireOp",EDGE,"E23.MirrorCS"),sQuery(id+"F0.wireOp",EDGE,"E24.trimOffspring"),sQuery(id+"F0.wireOp",EDGE,"E25.trimOffspring"),sQuery(id+"F0.wireOp",EDGE,"E26.trimOffspring"),sQuery(id+"F0.wireOp",EDGE,"E27.trimOffspring")])],"isStart":true});
            var sketch = newSketch(context, id + "F6", { "sketchPlane" : qUnion([Q0])});
            skLineSegment(sketch, "E78.0", {"start": v(-20, 55) * mm, "end": v(-55, 55) * mm});
            skLineSegment(sketch, "E79.0", {"start": v(-20, 55) * mm, "end": v(0, 80) * mm});
            skLineSegment(sketch, "E80.0", {"start": v(0, 80) * mm, "end": v(20, 55) * mm});
            skLineSegment(sketch, "E81.0", {"start": v(55, 55) * mm, "end": v(20, 55) * mm});
            skPoint(sketch, "E82.0", {"position": v(55, 37.5) * mm});
            skLineSegment(sketch, "E83.0", {"start": v(55, 20) * mm, "end": v(55, 55) * mm});
            skLineSegment(sketch, "E84.0", {"start": v(55, 20) * mm, "end": v(80, 0) * mm});
            skLineSegment(sketch, "E85.0", {"start": v(55, -20) * mm, "end": v(80, 0) * mm});
            skLineSegment(sketch, "E86.0", {"start": v(55, -55) * mm, "end": v(55, -20) * mm});
            skLineSegment(sketch, "E87.0", {"start": v(55, -55) * mm, "end": v(20, -55) * mm});
            skLineSegment(sketch, "E88.0", {"start": v(0, -80) * mm, "end": v(20, -55) * mm});
            skLineSegment(sketch, "E89.0", {"start": v(-20, -55) * mm, "end": v(0, -80) * mm});
            skLineSegment(sketch, "E90.0", {"start": v(-20, -55) * mm, "end": v(-55, -55) * mm});
            skLineSegment(sketch, "E91.0", {"start": v(-55, -55) * mm, "end": v(-55, -20) * mm});
            skLineSegment(sketch, "E92.0", {"start": v(-55, -20) * mm, "end": v(-80, 0) * mm});
            skLineSegment(sketch, "E93.0", {"start": v(-55, 20) * mm, "end": v(-80, 0) * mm});
            skLineSegment(sketch, "E94.0", {"start": v(-55, 20) * mm, "end": v(-55, 55) * mm});
            skLineSegment(sketch, "E95.0", {"start": v(-29, -12.5) * mm, "end": v(-29, 12.5) * mm});
            skLineSegment(sketch, "E96.0", {"start": v(-17, -12.5) * mm, "end": v(-17, 12.5) * mm});
            skLineSegment(sketch, "E97.0", {"start": v(-17, 12.5) * mm, "end": v(-29, 12.5) * mm});
            skLineSegment(sketch, "E98.0", {"start": v(-17, -12.5) * mm, "end": v(-29, -12.5) * mm});
            skLineSegment(sketch, "E99.0", {"start": v(29, -12.5) * mm, "end": v(17, -12.5) * mm});
            skLineSegment(sketch, "E100.0", {"start": v(29, -12.5) * mm, "end": v(29, 12.5) * mm});
            skLineSegment(sketch, "E101.0", {"start": v(17, 12.5) * mm, "end": v(29, 12.5) * mm});
            skLineSegment(sketch, "E102.0", {"start": v(17, -12.5) * mm, "end": v(17, 12.5) * mm});
            skCircle(sketch, "E103.0", {"center": v(23, -30) * mm, "radius": 3.5 * mm});
            skCircle(sketch, "E104.0", {"center": v(-23, -30) * mm, "radius": 3.5 * mm});
            skCircle(sketch, "E105.0", {"center": v(-23, 30) * mm, "radius": 3.5 * mm});
            skCircle(sketch, "E106.0", {"center": v(23, 30) * mm, "radius": 3.5 * mm});
            skSolve(sketch);
        }
        {
            var Q0;
            Q0 = qSketchRegion(id + "F6", true);
            extrude(context, id + "F7", {"entities" : qUnion([Q0]), "operationType" : NewBodyOperationType.ADD, "depth" : 5 * mm});
        }
    });
